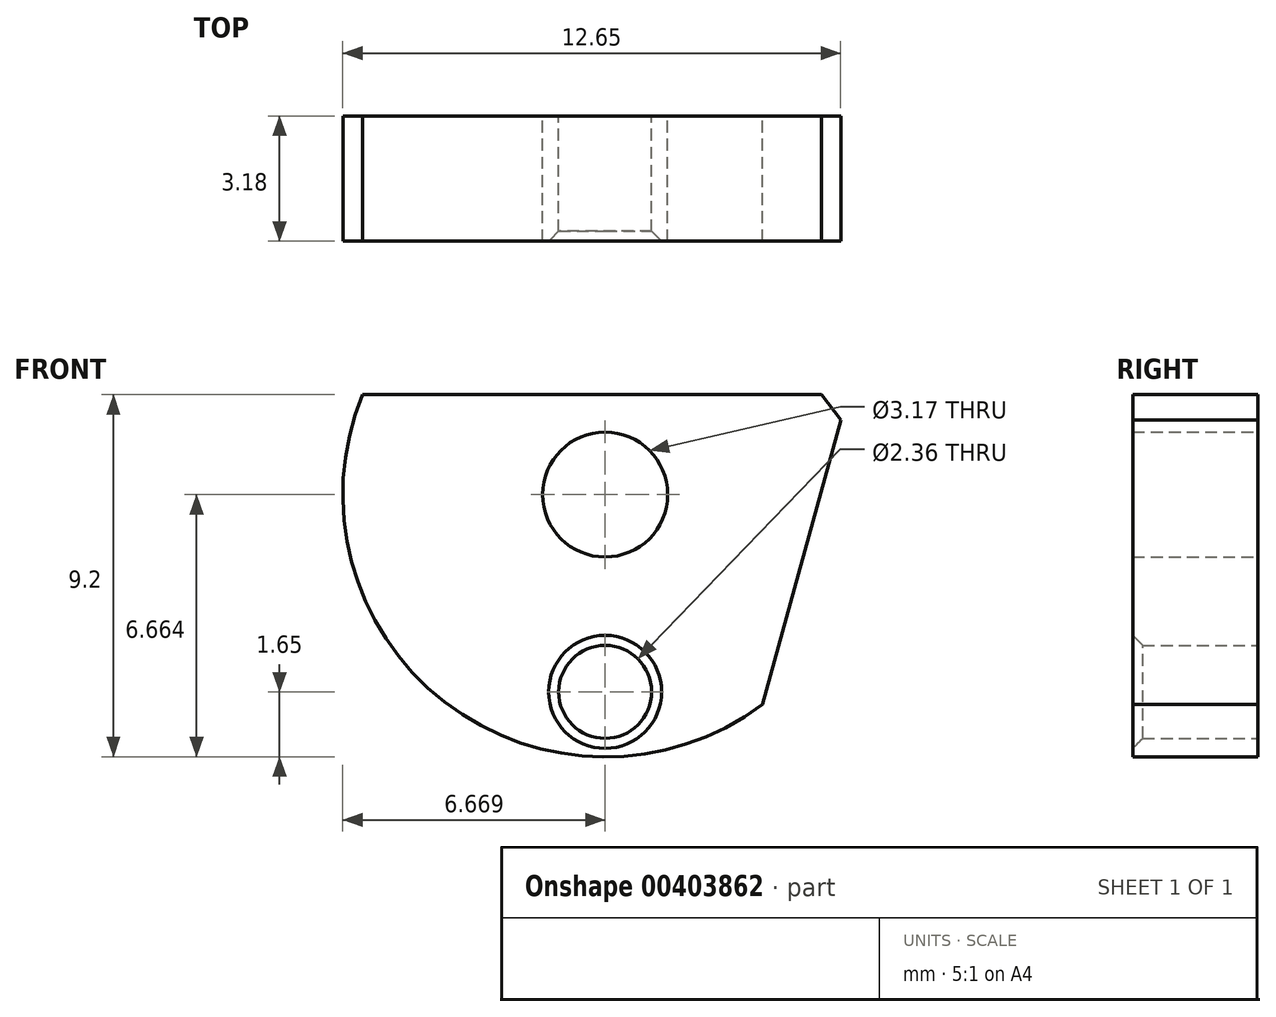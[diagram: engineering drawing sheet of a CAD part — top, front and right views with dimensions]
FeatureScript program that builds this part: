
annotation { "Feature Type Name" : "Feature", "Feature Type Description" : "" }
export const myFeature = defineFeature(function(context is Context, id is Id, definition is map)
    precondition{}
    {
        {
            var Q0;
            Q0=qCreatedBy(makeId("Front.planeOp"),FACE);
            var sketch = newSketch(context, id + "F0", { "sketchPlane" : qUnion([Q0])});
            skArc(sketch, "E0", {"start": v(-6.57, 4.1) * mm, "mid": v(-4.5, -3.71) * mm, "end": v(3.58, -3.78) * mm});
            skCircle(sketch, "E1", {"center": v(-0.41, 1.55) * mm, "radius": 1.59 * mm});
            skLineSegment(sketch, "E2", {"start": v(-6.57, 4.1) * mm, "end": v(5.75, 4.1) * mm});
            skCircle(sketch, "E3", {"center": v(-0.41, -3.46) * mm, "radius": 1.18 * mm});
            skLineSegment(sketch, "E4", {"start": v(5.75, 4.1) * mm, "end": v(3.58, -3.78) * mm});
            skSolve(sketch);
        }
        {
            var Q0;
            Q0=makeQuery(id+"F0.imprint","IMPRINT",FACE,{"disambiguationData":[TD([[makeQuery(id+"F0.imprint","IMPRINT",EDGE,{"derivedFrom":sQuery(id+"F0.wireOp",EDGE,"E0")}),1.0]])]});
            extrude(context, id + "F1", {"entities" : qUnion([Q0]), "endBound" : BoundingType.SYMMETRIC, "depth" : 3.17 * mm});
        }
        {
            var Q0;
            Q0=makeQuery(id+"F1.opExtrude","CAP_EDGE",EDGE,{"disambiguationData":[OSD([sQuery(id+"F0.wireOp",EDGE,"E3")])],"isStart":false});
            chamfer(context, id + "F2", {"entities" : qUnion([Q0]), "chamferType" : ChamferType.TWO_OFFSETS, "width1" : 0.25 * mm, "oppositeDirection" : false, "width2" : 0.25 * mm, "tangentPropagation" : true});
        }
        {
            var Q0;
            Q0=makeQuery(id+"F1.opExtrude","SWEPT_EDGE",EDGE,{"disambiguationData":[OSD([sQuery(id+"F0.wireOp",EDGE,"E2"),sQuery(id+"F0.wireOp",EDGE,"E4")])]});
            chamfer(context, id + "F3", {"entities" : qUnion([Q0]), "width" : 0.5 * mm, "tangentPropagation" : true});
        }
    });
